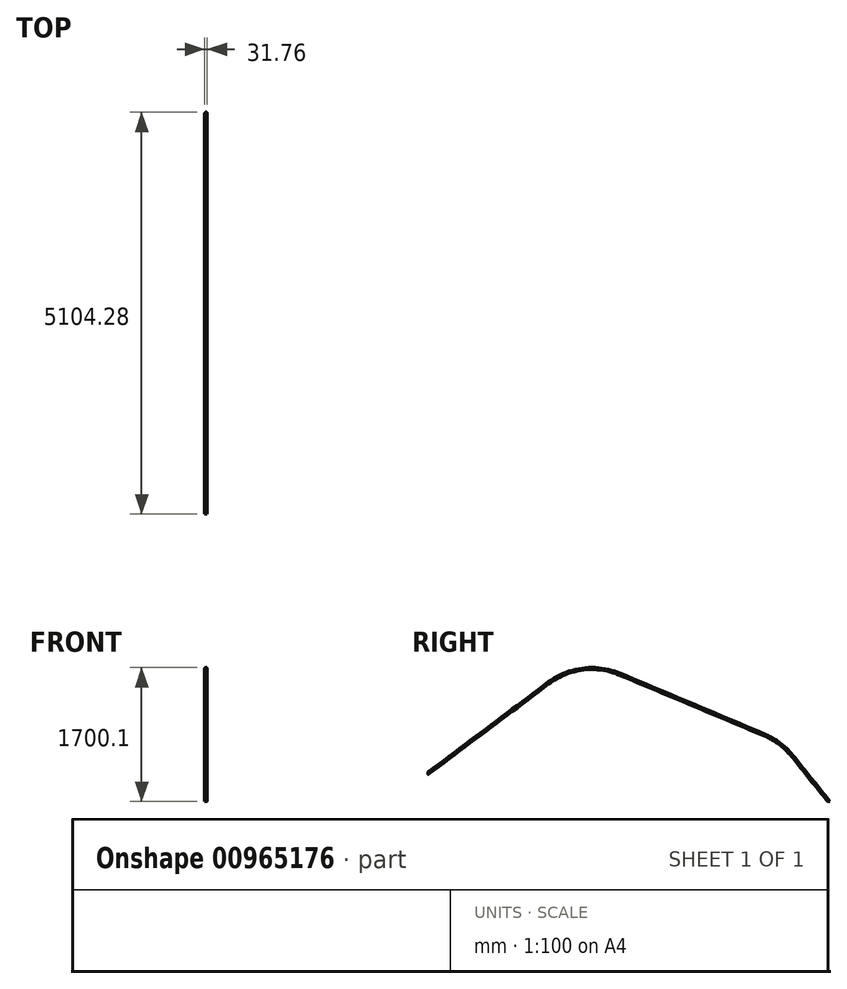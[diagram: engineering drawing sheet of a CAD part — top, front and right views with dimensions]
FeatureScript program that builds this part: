
annotation { "Feature Type Name" : "Feature", "Feature Type Description" : "" }
export const myFeature = defineFeature(function(context is Context, id is Id, definition is map)
    precondition{}
    {
        {
            var Q0;
            Q0=qCreatedBy(makeId("Front.planeOp"),FACE);
            var sketch = newSketch(context, id + "F0", { "sketchPlane" : qUnion([Q0])});
            skCircle(sketch, "E0", {"center": v(0, 0) * mm, "radius": 15.88 * mm});
            skCircle(sketch, "E1", {"center": v(0, 0) * mm, "radius": 12.7 * mm});
            skSolve(sketch);
        }
        {
            var Q0;
            Q0=qCreatedBy(makeId("Right.planeOp"),FACE);
            var sketch = newSketch(context, id + "F1", { "sketchPlane" : qUnion([Q0])});
            skLineSegment(sketch, "E2", {"start": v(0, 0) * mm, "end": v(1531.97, 1147.94) * mm});
            skLineSegment(sketch, "E3", {"start": v(2434.5, 1259.19) * mm, "end": v(4268.56, 488.58) * mm});
            skLineSegment(sketch, "E4", {"start": v(4627.4, 218.01) * mm, "end": v(5088.42, -356.24) * mm});
            skPoint(sketch, "E5.visualSharp", {"position": v(1951.36, 1462.19) * mm});
            skArc(sketch, "E5.filletArc", {"start": v(2434.5, 1259.19) * mm, "mid": v(1968.43, 1323.7) * mm, "end": v(1531.97, 1147.94) * mm});
            skPoint(sketch, "E6.visualSharp", {"position": v(4482.27, 398.78) * mm});
            skArc(sketch, "E6.filletArc", {"start": v(4627.4, 218.01) * mm, "mid": v(4464.86, 375.68) * mm, "end": v(4268.56, 488.58) * mm});
            skSolve(sketch);
        }
        {
            var Q0;
            Q0=makeQuery(id+"F0.imprint","IMPRINT",FACE,{"disambiguationData":[TD([[makeQuery(id+"F0.imprint","IMPRINT",EDGE,{"derivedFrom":sQuery(id+"F0.wireOp",EDGE,"E0")}),1.0]])]});
            var Q1;
            Q1=sQuery(id+"F0.wireOp",EDGE,"E0");
            var Q2;
            Q2=sQuery(id+"F1.wireOp",EDGE,"E2");
            var Q3;
            Q3=sQuery(id+"F1.wireOp",EDGE,"E5.filletArc");
            var Q4;
            Q4=sQuery(id+"F1.wireOp",EDGE,"E3");
            var Q5;
            Q5=sQuery(id+"F1.wireOp",EDGE,"E6.filletArc");
            var Q6;
            Q6=sQuery(id+"F1.wireOp",EDGE,"E4");
            sweep(context, id + "F2", {"profiles" : qUnion([Q0]), "surfaceProfiles" : qUnion([Q1]), "path" : qUnion([Q2, Q3, Q4, Q5, Q6])});
        }
    });
